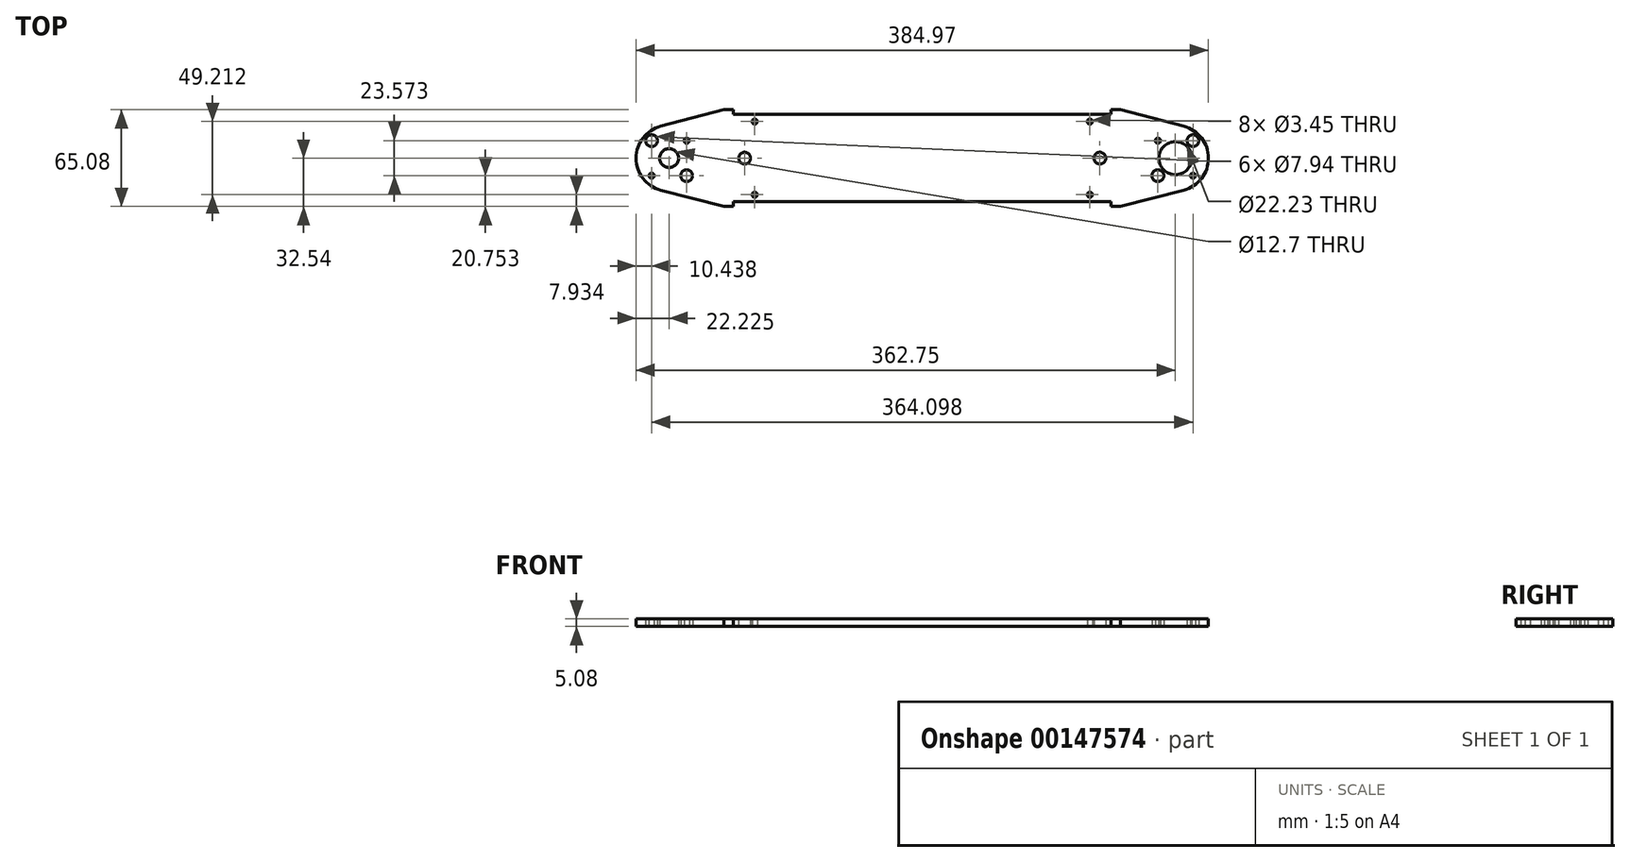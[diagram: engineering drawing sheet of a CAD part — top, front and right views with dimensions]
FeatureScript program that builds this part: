
annotation { "Feature Type Name" : "Feature", "Feature Type Description" : "" }
export const myFeature = defineFeature(function(context is Context, id is Id, definition is map)
    precondition{}
    {
        {
            var Q0;
            Q0=qCreatedBy(makeId("Top.planeOp"),FACE);
            var sketch = newSketch(context, id + "F0", { "sketchPlane" : qUnion([Q0])});
            skPoint(sketch, "E0.rect.middle", {"position": v(0, 0) * mm});
            skCircle(sketch, "E1", {"center": v(0, 0) * mm, "radius": 11.11 * mm});
            skLineSegment(sketch, "E2.bottom", {"start": v(11.79, 11.79) * mm, "end": v(-11.79, 11.79) * mm, "construction": true});
            skLineSegment(sketch, "E2.left", {"start": v(11.79, 11.79) * mm, "end": v(11.79, -11.79) * mm, "construction": true});
            skLineSegment(sketch, "E2.right", {"start": v(-11.79, 11.79) * mm, "end": v(-11.79, -11.79) * mm, "construction": true});
            skCircle(sketch, "E3", {"center": v(11.79, 11.79) * mm, "radius": 5.56 * mm, "construction": true});
            skCircle(sketch, "E4", {"center": v(-11.79, 11.79) * mm, "radius": 1.73 * mm});
            skCircle(sketch, "E5", {"center": v(11.79, 11.79) * mm, "radius": 3.97 * mm});
            skCircle(sketch, "E6", {"center": v(11.79, -11.79) * mm, "radius": 1.73 * mm});
            skCircle(sketch, "E7", {"center": v(-11.79, -11.79) * mm, "radius": 3.97 * mm});
            skArc(sketch, "E8", {"start": v(-346.1, 21.51) * mm, "mid": v(-362.75, 0) * mm, "end": v(-346.1, -21.51) * mm});
            skLineSegment(sketch, "E9.bottom", {"start": v(-352.31, 11.79) * mm, "end": v(-328.74, 11.79) * mm, "construction": true});
            skLineSegment(sketch, "E9.top", {"start": v(-352.31, -11.79) * mm, "end": v(-328.74, -11.79) * mm, "construction": true});
            skLineSegment(sketch, "E9.left", {"start": v(-352.31, 11.79) * mm, "end": v(-352.31, -11.79) * mm, "construction": true});
            skLineSegment(sketch, "E9.right", {"start": v(-328.74, 11.79) * mm, "end": v(-328.74, -11.79) * mm, "construction": true});
            skCircle(sketch, "E10", {"center": v(-328.74, 11.79) * mm, "radius": 1.73 * mm});
            skCircle(sketch, "E11", {"center": v(-340.53, 0) * mm, "radius": 6.35 * mm});
            skCircle(sketch, "E12", {"center": v(-352.31, 11.79) * mm, "radius": 3.97 * mm});
            skCircle(sketch, "E13", {"center": v(-352.31, -11.79) * mm, "radius": 1.73 * mm});
            skCircle(sketch, "E14", {"center": v(-328.74, -11.79) * mm, "radius": 3.97 * mm});
            skLineSegment(sketch, "E15", {"start": v(0, 0) * mm, "end": v(-340.53, 0) * mm, "construction": true});
            skLineSegment(sketch, "E16", {"start": v(-346.1, -21.51) * mm, "end": v(-303.61, -32.54) * mm});
            skLineSegment(sketch, "E17", {"start": v(-346.1, 21.51) * mm, "end": v(-303.61, 32.54) * mm});
            skLineSegment(sketch, "E18", {"start": v(-297.26, -29.37) * mm, "end": v(-43.26, -29.37) * mm});
            skLineSegment(sketch, "E19", {"start": v(-297.26, 29.37) * mm, "end": v(-43.26, 29.37) * mm});
            skLineSegment(sketch, "E20", {"start": v(-297.26, 32.54) * mm, "end": v(-297.26, 29.37) * mm});
            skLineSegment(sketch, "E21", {"start": v(-297.26, 32.54) * mm, "end": v(-303.61, 32.54) * mm});
            skLineSegment(sketch, "E22", {"start": v(-297.26, -29.37) * mm, "end": v(-297.26, -32.54) * mm});
            skLineSegment(sketch, "E23", {"start": v(-297.26, -32.54) * mm, "end": v(-303.61, -32.54) * mm});
            skLineSegment(sketch, "E24", {"start": v(-43.26, -29.37) * mm, "end": v(-43.26, -32.54) * mm});
            skLineSegment(sketch, "E25", {"start": v(-43.26, -32.54) * mm, "end": v(-36.91, -32.54) * mm});
            skLineSegment(sketch, "E26", {"start": v(-43.26, 29.37) * mm, "end": v(-43.26, 32.54) * mm});
            skLineSegment(sketch, "E27", {"start": v(-43.26, 32.54) * mm, "end": v(-36.91, 32.54) * mm});
            skLineSegment(sketch, "E28", {"start": v(-36.91, -32.54) * mm, "end": v(5.58, -21.51) * mm});
            skLineSegment(sketch, "E29", {"start": v(5.58, 21.51) * mm, "end": v(-36.91, 32.54) * mm});
            skArc(sketch, "E30", {"start": v(5.58, -21.51) * mm, "mid": v(22.23, 0) * mm, "end": v(5.58, 21.51) * mm});
            skLineSegment(sketch, "E31", {"start": v(-297.26, 29.37) * mm, "end": v(-297.26, 24.6) * mm, "construction": true});
            skLineSegment(sketch, "E32", {"start": v(-297.26, 24.6) * mm, "end": v(-282.98, 24.6) * mm, "construction": true});
            skLineSegment(sketch, "E33", {"start": v(-297.26, -29.37) * mm, "end": v(-297.26, -24.6) * mm, "construction": true});
            skLineSegment(sketch, "E34", {"start": v(-297.26, -24.6) * mm, "end": v(-282.98, -24.6) * mm, "construction": true});
            skLineSegment(sketch, "E35", {"start": v(-43.26, -29.37) * mm, "end": v(-43.26, -24.6) * mm, "construction": true});
            skLineSegment(sketch, "E36", {"start": v(-43.26, -24.6) * mm, "end": v(-57.55, -24.6) * mm, "construction": true});
            skLineSegment(sketch, "E37", {"start": v(-43.26, 29.37) * mm, "end": v(-43.26, 24.6) * mm, "construction": true});
            skLineSegment(sketch, "E38", {"start": v(-43.26, 24.6) * mm, "end": v(-57.55, 24.6) * mm, "construction": true});
            skCircle(sketch, "E39", {"center": v(-282.98, 24.6) * mm, "radius": 1.73 * mm});
            skCircle(sketch, "E40", {"center": v(-57.55, 24.6) * mm, "radius": 1.73 * mm});
            skCircle(sketch, "E41", {"center": v(-57.55, -24.6) * mm, "radius": 1.73 * mm});
            skCircle(sketch, "E42", {"center": v(-282.98, -24.6) * mm, "radius": 1.73 * mm});
            skLineSegment(sketch, "E43", {"start": v(-11.79, -11.79) * mm, "end": v(11.79, -11.79) * mm, "construction": true});
            skLineSegment(sketch, "E44", {"start": v(-170.26, -29.37) * mm, "end": v(-170.26, 0) * mm, "construction": true});
            skLineSegment(sketch, "E45", {"start": v(-170.26, 0) * mm, "end": v(-170.26, 29.37) * mm, "construction": true});
            skLineSegment(sketch, "E46", {"start": v(-328.74, 11.79) * mm, "end": v(-289.73, 11.79) * mm, "construction": true});
            skLineSegment(sketch, "E47", {"start": v(-289.73, 11.79) * mm, "end": v(-289.73, 0) * mm, "construction": true});
            skLineSegment(sketch, "E48", {"start": v(-11.79, 11.79) * mm, "end": v(-50.8, 11.79) * mm, "construction": true});
            skLineSegment(sketch, "E49", {"start": v(-50.8, 11.79) * mm, "end": v(-50.8, 0) * mm, "construction": true});
            skCircle(sketch, "E50", {"center": v(-50.8, 0) * mm, "radius": 3.97 * mm});
            skCircle(sketch, "E51", {"center": v(-289.73, 0) * mm, "radius": 3.97 * mm});
            skSolve(sketch);
        }
        {
            var Q0;
            Q0=qSketchRegion(id+"F0",true);
            extrude(context, id + "F1", {"entities" : qUnion([Q0]), "depth" : 5.08 * mm});
        }
    });
